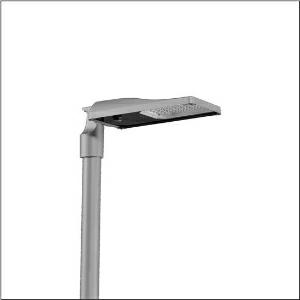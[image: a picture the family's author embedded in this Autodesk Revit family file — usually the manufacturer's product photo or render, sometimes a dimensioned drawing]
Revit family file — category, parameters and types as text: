
# Revit family: streetlight_sl_31_mini___st1_0a_5xh2d3ar08ha_7279
name_source: partatom
category: Lighting Fixtures
units: mm (PartAtom-declared; Revit-internal decimal feet)

## family parameters
Cut with Voids When Loaded = No
Host = Face
Light Source = No
Part Type = Normal
Room Calculation Point = No
Round Connector Dimension = Use Diameter
Shared = No

## types (1)
- --- (1 x LED, 9230 lm, 68.3 W, 3000K)
    Apparent Load = 68 VA
    CIE Flux Codes = 37 72 97 100 100
    Color Rendering = 70
    Color Temperature = 3000K
    Default Elevation = 1800 mm
    Description = Streetlight SL 31 mini D4i mast luminaire for post-top, side-entry; light control with lens of PMMA; light distribution: ST1.0a, direct asymmetric distribution, for standard-compliant lighting for roads and squares; LED: luminous flux: 9.230lm, light colour: 730, colour temperature: 3000K; luminous efficacy: 135,1lm/W; control: pre-setting: logarithmic dimming characteristic, flexible luminous flux parameterisation, time-dependent luminous flux control, constant luminous flux control, power reduction, intelligent temperature release in ECG and LED module, overheat protection; luminaire housing, of diecast aluminium, Siteco® metallic grey (DB 702S), corrosivity category C5 high according to DIN EN ISO 12944; cover of toughened safety glass, transparent, mast flange of diecast aluminium, Siteco® metallic grey (DB 702S), spigot size: 76/60mm, mast flange included unmounted; with cable H07RN-F 2x 1.5mm², cable length: 8,5m, connection cable pre-assembled; mains connection: 220..240V, AC, 50/60Hz; power consumption (at start of service life): 68,3W / (at end of service life): 74,5W / (with reduced operation 50%): 29,5W; protection rating (complete): IP66; insulation class (complete): insulation class II (safety insulation); impact resistance: IK09; certification: CE, ENEC, ENEC+, VDE, UKCA, ZD4i; permissible operating ambient temperature for outdoor applications: -40..+50°C; packaging unit: 1 piece

Light Distribution: ST1.0a
    Height = 76 mm
    Lamp = 1 x LED
    Lamp Light Flux = 9230 lm
    Lamp Power = 68.3 W
    Lamp count = 1
    Length = 547 mm
    Luminous efficacy = 135 lm/W
    Manufacturer = Siteco
    ModVariant = No
    Model = 5XH2D3AR08HA
    Number of Poles = 1
    OnlyDefault = Yes
    Power Factor = 1
    Product Name = Streetlight SL 31 mini | ST1.0a
    Product group = mast luminaire | pylon top
    ProductGroupID = 6100
    Protection Class = Protection class II
    Protection Degree = IP 66
    RLX_Detail_Level = 1
    RLX_Emergency_Light_Flux = 0 lm
    RLX_Emergency_Type = 0
    RLX_Emergency_Type_DB = No
    RlxData = <blob elided: 24193 chars, md5=9ffc67e5>
    Socket = socket
    Standby Power = 0 W
    System Light Flux = 9230 lm
    System Power = 68 W
    Type Comments = factory setting: luminous flux: 100 % | dim-lin: 254 | 692 mA
    Type Image = l_1300328.jpg
    URL = http://relux.com
    VarID = @adj_002363
    Voltage = 0 V
    Weight = 0.00 kg
    Width = 265 mm

## geometry (parser evidence)
native form markers: Blend x4, Sweep x10
no freeform markers — native parametric forms only
